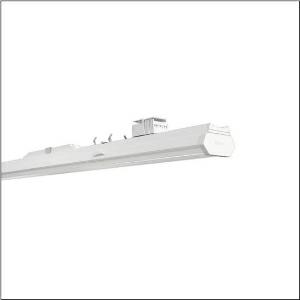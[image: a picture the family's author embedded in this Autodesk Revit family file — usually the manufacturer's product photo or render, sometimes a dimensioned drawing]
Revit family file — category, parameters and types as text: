
# Revit family: licross_r__21_protected_mo_52ts12cn67xf_4b2a
name_source: partatom
category: Lighting Fixtures
units: mm (PartAtom-declared; Revit-internal decimal feet)

## family parameters
Cut with Voids When Loaded = No
Host = Face
Light Source = No
Part Type = Normal
Room Calculation Point = No
Round Connector Dimension = Use Diameter
Shared = No

## types (1)
- --- (1 x LED, 7470 lm, 48.5 W, 6500K)
    Apparent Load = 49 VA
    CIE Flux Codes = 54 82 95 97 100
    Color Rendering = 80
    Color Temperature = 6500K
    Default Elevation = 1800 mm
    Description = Licross® 21 Protected MO, luminaire insert, of sheet steel, galvanised, coil coated, white, length: 1.500mm, width: 90mm, height: 101mm, LED rated luminous flux: 7.460lm, light colour: 865, control gear: ON/OFF Multilumen, CLOi, control gear: ECG Multilumen, with plug, 3-pole, with phase selection, mains connection: 220..240V, AC, 50/60Hz, halogen-free wiring, primary optical cover: cover, of PMMA, light emission: direct with ceiling illumination distribution, protection rating (complete): IP50, insulation class (complete): insulation class I (protective earthing), certification: CE, ENEC, VDE, UKCA, protection symbol: D if used in an environment with conductive dust loads with corresponding accessories, permissible ambient temperature for indoor applications: -35..+45°C, corresponds to IFS (International Featured Standards) requirements for safety and quality in the food industry, reducing of maximum allowable ambient temperature of 5°C with ceiling mounting, LABS conformity tested according to VDMA 24364:2018-05, packaging unit: 1 piece
    Height = 92 mm
    Lamp = 1 x LED
    Lamp Light Flux = 7470 lm
    Lamp Power = 48.5 W
    Lamp count = 1
    Length = 1500 mm
    Luminous efficacy = 154 lm/W
    Manufacturer = Siteco
    ModVariant = No
    Model = 52TS12CN67XF
    Mounting Place = Ceiling
    Mounting Type = Pendant
    Number of Poles = 1
    OnlyDefault = Yes
    Power Factor = 1
    Product Name = Licross® 21 Protected MO
    Product group = luminaire insert
    ProductGroupID = 902
    Protection Class = Protection class I
    Protection Degree = IP 50
    RLX_Detail_Level = 1
    RlxData = <blob elided: 21861 chars, md5=27d3aa92>
    Socket = socket
    Standby Power = 0 W
    System Light Flux = 7470 lm
    System Power = 49 W
    Type Comments = factory setting: luminous flux: 100 % | (A | C | E) | 117 mA
    Type Image = l_1256145.jpg
    URL = http://relux.com
    VarID = @adj_118531
    Voltage = 0 V
    Weight = 0.00 kg
    Width = 88 mm

## geometry (parser evidence)
native form markers: Blend x4, Sweep x12
no freeform markers — native parametric forms only
